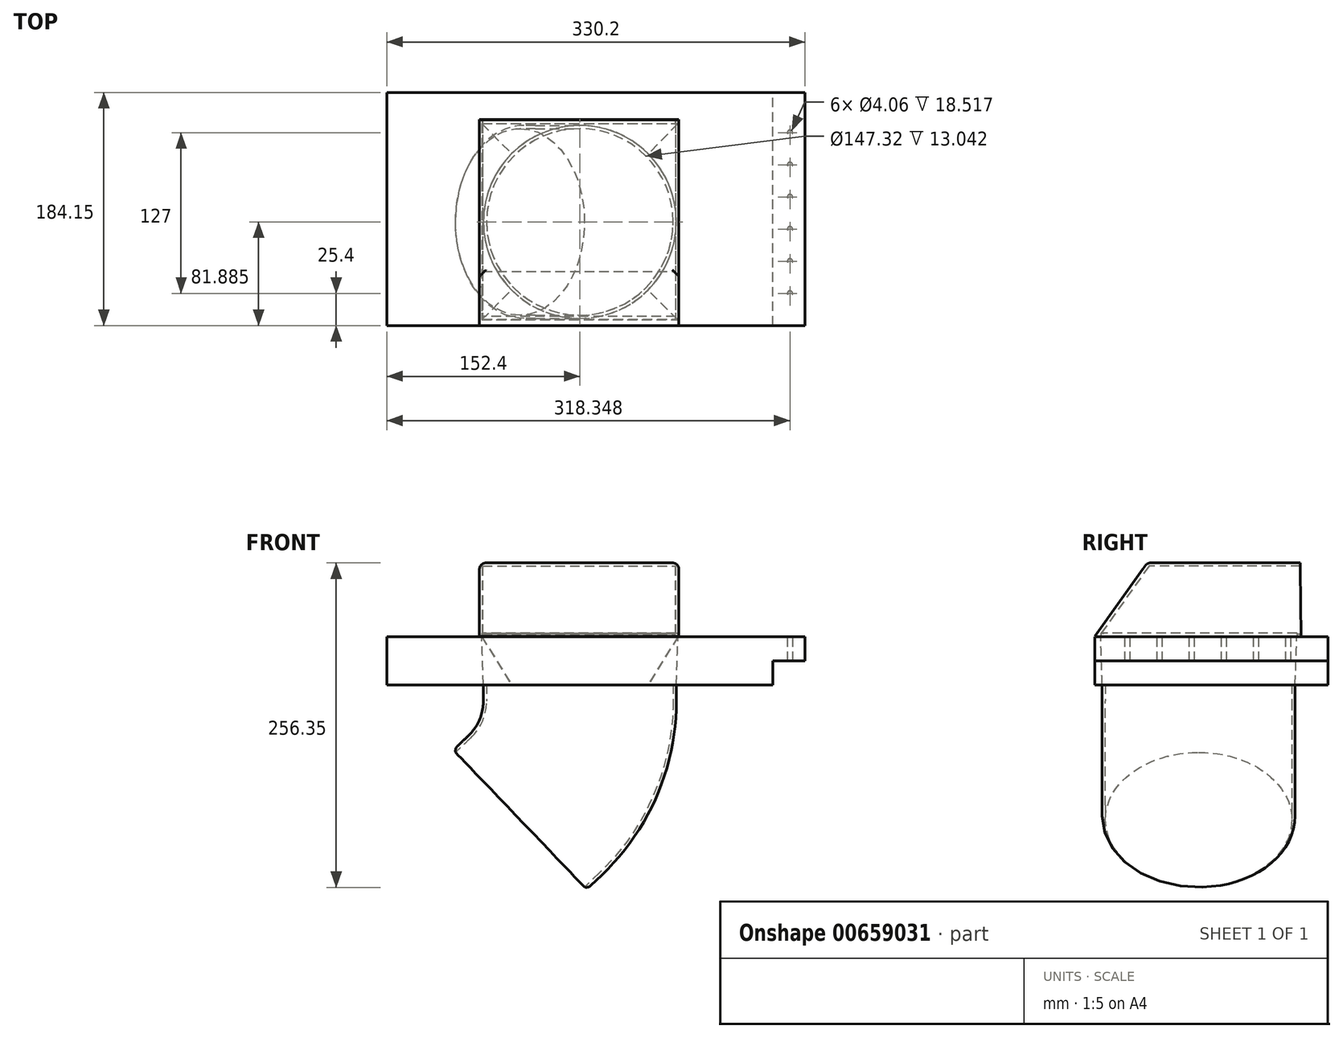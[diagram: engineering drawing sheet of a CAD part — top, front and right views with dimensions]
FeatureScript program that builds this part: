
annotation { "Feature Type Name" : "Feature", "Feature Type Description" : "" }
export const myFeature = defineFeature(function(context is Context, id is Id, definition is map)
    precondition{}
    {
        {
            var Q0;
            Q0=qCreatedBy(makeId("Front.planeOp"),FACE);
            var sketch = newSketch(context, id + "F0", { "sketchPlane" : qUnion([Q0])});
            skLineSegment(sketch, "E0.bottom", {"start": v(0, 0) * mm, "end": v(-304.8, 0) * mm});
            skLineSegment(sketch, "E0.top", {"start": v(0, 38.1) * mm, "end": v(-304.8, 38.1) * mm});
            skLineSegment(sketch, "E0.left", {"start": v(0, 0) * mm, "end": v(0, 38.1) * mm});
            skLineSegment(sketch, "E0.right", {"start": v(-304.8, 0) * mm, "end": v(-304.8, 38.1) * mm});
            skSolve(sketch);
        }
        {
            var Q0;
            Q0=makeQuery(id+"F0.imprint","IMPRINT",FACE,{"disambiguationData":[TD([[makeQuery(id+"F0.imprint","IMPRINT",EDGE,{"derivedFrom":sQuery(id+"F0.wireOp",EDGE,"E0.bottom")}),-1.0]])]});
            extrude(context, id + "F1", {"entities" : qUnion([Q0]), "depth" : 184.15 * mm, "offsetDistance" : 25.4 * mm});
        }
        {
            var Q0;
            Q0=makeQuery(id+"F1.opExtrude","SWEPT_FACE",FACE,{"disambiguationData":[OSD([sQuery(id+"F0.wireOp",EDGE,"E0.bottom")])]});
            var sketch = newSketch(context, id + "F2", { "sketchPlane" : qUnion([Q0])});
            skLineSegment(sketch, "E1", {"start": v(-304.8, 25.4) * mm, "end": v(0, 25.4) * mm, "construction": true});
            skLineSegment(sketch, "E2", {"start": v(-152.4, 0) * mm, "end": v(-152.4, 184.15) * mm, "construction": true});
            skCircle(sketch, "E3", {"center": v(-152.4, 102.27) * mm, "radius": 76.2 * mm});
            skSolve(sketch);
        }
        {
            var Q0;
            Q0=makeQuery(id+"F1.opExtrude","SWEPT_FACE",FACE,{"disambiguationData":[OSD([sQuery(id+"F0.wireOp",EDGE,"E0.top")])]});
            var sketch = newSketch(context, id + "F3", { "sketchPlane" : qUnion([Q0])});
            skLineSegment(sketch, "E4.bottom", {"start": v(-229.83, -24.64) * mm, "end": v(-74.9, -24.64) * mm});
            skLineSegment(sketch, "E4.top", {"start": v(-229.83, -179.58) * mm, "end": v(-74.9, -179.58) * mm});
            skLineSegment(sketch, "E4.left", {"start": v(-229.83, -24.64) * mm, "end": v(-229.83, -179.58) * mm});
            skLineSegment(sketch, "E4.right", {"start": v(-74.9, -24.64) * mm, "end": v(-74.9, -179.58) * mm});
            skSolve(sketch);
        }
        {
            var Q0;
            Q0=qCreatedBy(makeId("Right.planeOp"),FACE);
            cPlane(context, id + "F4", {"entities" : qUnion([Q0]), "cplaneType" : CPlaneType.OFFSET, "offset" : 74.17 * mm, "oppositeDirection" : true, "width" : 152.4 * mm, "height" : 152.4 * mm});
        }
        {
            var Q0;
            Q0=qCreatedBy(id+"F4.planeOp",FACE);
            var sketch = newSketch(context, id + "F5", { "sketchPlane" : qUnion([Q0])});
            skLineSegment(sketch, "E5", {"start": v(-21.5, 37.62) * mm, "end": v(-21.85, 96.32) * mm});
            skLineSegment(sketch, "E6", {"start": v(-21.85, 96.32) * mm, "end": v(-142.8, 96.32) * mm});
            skLineSegment(sketch, "E7", {"start": v(-142.8, 96.32) * mm, "end": v(-184.14, 38.21) * mm});
            skLineSegment(sketch, "E8", {"start": v(-184.14, 38.21) * mm, "end": v(-21.5, 37.62) * mm});
            skSolve(sketch);
        }
        {
            var Q0;
            Q0=qSketchRegion(id+"F5",true);
            extrude(context, id + "F6", {"entities" : qUnion([Q0]), "operationType" : NewBodyOperationType.ADD, "oppositeDirection" : true, "depth" : 157.48 * mm, "offsetDistance" : 25.4 * mm});
        }
        {
            var Q0;
            Q0=makeQuery(id+"F6.opExtrude","SWEPT_FACE",FACE,{"disambiguationData":[OSD([sQuery(id+"F5.wireOp",EDGE,"E5")])]});
            shell(context, id + "F7", {"entities" : qUnion([Q0]), "thickness" : 2.54 * mm});
        }
        {
            var Q1;
            Q1=qSketchRegion(id+"F3",true);
            var Q2;
            Q2=qSketchRegion(id+"F2",true);
            loft(context, id + "F8", {"operationType" : NewBodyOperationType.REMOVE, "sheetProfilesArray" : [{ "sheetProfileEntities" : qUnion([Q1]) }, { "sheetProfileEntities" : qUnion([Q2]) }]});
        }
        {
            var Q0;
            Q0=qSketchRegion(id+"F3",true);
            extrude(context, id + "F9", {"entities" : qUnion([Q0]), "operationType" : NewBodyOperationType.REMOVE, "depth" : 2.62 * mm, "offsetDistance" : 25.4 * mm});
        }
        {
            var Q0;
            Q0=qCreatedBy(makeId("Front.planeOp"),FACE);
            cPlane(context, id + "F10", {"entities" : qUnion([Q0]), "cplaneType" : CPlaneType.OFFSET, "offset" : 102.36 * mm, "width" : 152.4 * mm, "height" : 152.4 * mm});
        }
        {
            var Q0;
            Q0=qCreatedBy(id+"F10.planeOp",FACE);
            var sketch = newSketch(context, id + "F11", { "sketchPlane" : qUnion([Q0])});
            skLineSegment(sketch, "E9", {"start": v(-78.95, 0) * mm, "end": v(-228.5, 0) * mm, "construction": true});
            skLineSegment(sketch, "E10", {"start": v(-153.72, 0) * mm, "end": v(-153.72, -12.7) * mm});
            skPoint(sketch, "E11.visualSharp", {"position": v(-153.72, -76.2) * mm});
            skArc(sketch, "E12", {"start": v(-188.52, -94.16) * mm, "mid": v(-162.78, -56.99) * mm, "end": v(-153.72, -12.7) * mm});
            skLineSegment(sketch, "E13", {"start": v(-188.52, -94.16) * mm, "end": v(-200.52, -105.65) * mm});
            skLineSegment(sketch, "E14", {"start": v(-153.72, 0) * mm, "end": v(-153.72, 0.34) * mm});
            skSolve(sketch);
        }
        {
            var Q0;
            Q0=qSketchRegion(id+"F2",true);
            var Q1;
            Q1=qConstructionFilter(qBodyType(qCreatedBy(id+"F11",EDGE),BodyType.WIRE),ConstructionObject.NO);
            sweep(context, id + "F12", {"profiles" : qUnion([Q0]), "path" : qUnion([Q1])});
        }
        {
            var Q0;
            Q0=makeQuery(id+"F12.opSweep","CAP_FACE",FACE,{"disambiguationData":[OSD([sQuery(id+"F2.wireOp",EDGE,"E3"),sQuery(id+"F11.wireOp",VERTEX,"PWPHreBG-1Q1P-dGp8-n0dr-esqENqL7WHNy.end")])],"isStart":false});
            var Q1;
            Q1=makeQuery(id+"F12.opSweep","CAP_FACE",FACE,{"disambiguationData":[OSD([sQuery(id+"F2.wireOp",EDGE,"E3"),sQuery(id+"F11.wireOp",VERTEX,"E10.start")])],"isStart":true});
            var Q2;
            Q2=makeQuery(id+"F12.opSweep","SWEPT_BODY",BODY,{"disambiguationData":[OSD([sQuery(id+"F2.wireOp",EDGE,"E3"),sQuery(id+"F11.wireOp",EDGE,"E10")])]});
            shell(context, id + "F13", {"entities" : qUnion([Q0, Q1]), "parts" : qUnion([Q2]), "thickness" : 2.54 * mm});
        }
        {
            var Q0;
            Q0=makeQuery(id+"F6.opExtrude","CAP_EDGE",EDGE,{"disambiguationData":[OSD([sQuery(id+"F5.wireOp",EDGE,"E6")])],"isStart":true});
            var Q1;
            Q1=makeQuery(id+"F6.opExtrude","SWEPT_EDGE",EDGE,{"disambiguationData":[OSD([sQuery(id+"F5.wireOp",EDGE,"E6"),sQuery(id+"F5.wireOp",EDGE,"E7")])]});
            var Q2;
            Q2=makeQuery(id+"F6.opExtrude","CAP_EDGE",EDGE,{"disambiguationData":[OSD([sQuery(id+"F5.wireOp",EDGE,"E6")])],"isStart":false});
            fillet(context, id + "F14", {"entities" : qUnion([Q0, Q1, Q2]), "radius" : 5.08 * mm, "tangentPropagation" : true, "allowEdgeOverflow" : false});
        }
        {
            var Q0;
            Q0=makeQuery(id+"F12.opSweep","CAP_EDGE",EDGE,{"disambiguationData":[OSD([sQuery(id+"F2.wireOp",EDGE,"E3"),sQuery(id+"F11.wireOp",VERTEX,"PWPHreBG-1Q1P-dGp8-n0dr-esqENqL7WHNy.end")])],"isStart":false});
            fillet(context, id + "F15", {"entities" : qUnion([Q0]), "radius" : 5.08 * mm, "tangentPropagation" : true, "allowEdgeOverflow" : false});
        }
        {
            var Q0;
            Q0=makeQuery(id+"F1.opExtrude","SWEPT_FACE",FACE,{"disambiguationData":[OSD([sQuery(id+"F0.wireOp",EDGE,"E0.left")])]});
            var sketch = newSketch(context, id + "F16", { "sketchPlane" : qUnion([Q0])});
            skLineSegment(sketch, "E15.bottom", {"start": v(-184.15, 38.1) * mm, "end": v(0, 38.1) * mm});
            skLineSegment(sketch, "E15.top", {"start": v(-184.15, 19.05) * mm, "end": v(0, 19.05) * mm});
            skLineSegment(sketch, "E15.left", {"start": v(-184.15, 38.1) * mm, "end": v(-184.15, 19.05) * mm});
            skLineSegment(sketch, "E15.right", {"start": v(0, 38.1) * mm, "end": v(0, 19.05) * mm});
            skSolve(sketch);
        }
        {
            var Q0;
            Q0=makeQuery(id+"F16.imprint","IMPRINT",FACE,{"disambiguationData":[TD([[makeQuery(id+"F16.imprint","IMPRINT",EDGE,{"derivedFrom":sQuery(id+"F16.wireOp",EDGE,"E15.bottom")}),-1.0]])]});
            extrude(context, id + "F17", {"entities" : qUnion([Q0]), "operationType" : NewBodyOperationType.ADD, "depth" : 25.4 * mm, "offsetDistance" : 25.4 * mm});
        }
        {
            var Q0;
            Q0=makeQuery(id+"F17.opExtrude","SWEPT_FACE",FACE,{"disambiguationData":[OSD([sQuery(id+"F16.wireOp",EDGE,"E15.top")])]});
            var sketch = newSketch(context, id + "F18", { "sketchPlane" : qUnion([Q0])});
            skCircle(sketch, "E16", {"center": v(13.55, 158.75) * mm, "radius": 2.03 * mm});
            skCircle(sketch, "E17.0.1.0", {"center": v(13.55, 133.35) * mm, "radius": 2.03 * mm});
            skCircle(sketch, "E17.0.2.0", {"center": v(13.55, 107.95) * mm, "radius": 2.03 * mm});
            skCircle(sketch, "E17.0.3.0", {"center": v(13.55, 82.55) * mm, "radius": 2.03 * mm});
            skCircle(sketch, "E17.0.4.0", {"center": v(13.55, 57.15) * mm, "radius": 2.03 * mm});
            skCircle(sketch, "E17.0.5.0", {"center": v(13.55, 31.75) * mm, "radius": 2.03 * mm});
            skLineSegment(sketch, "E17.direction1", {"start": v(13.55, 158.75) * mm, "end": v(38.95, 158.75) * mm, "construction": true});
            skLineSegment(sketch, "E17.direction2", {"start": v(13.55, 158.75) * mm, "end": v(13.55, 133.35) * mm, "construction": true});
            skSolve(sketch);
        }
        {
            var Q0;
            Q0 = qSketchRegion(id + "F18", true);
            extrude(context, id + "F19", {"entities" : qUnion([Q0]), "operationType" : NewBodyOperationType.REMOVE, "oppositeDirection" : true, "depth" : 18.52 * mm, "offsetDistance" : 25.4 * mm});
        }
    });
